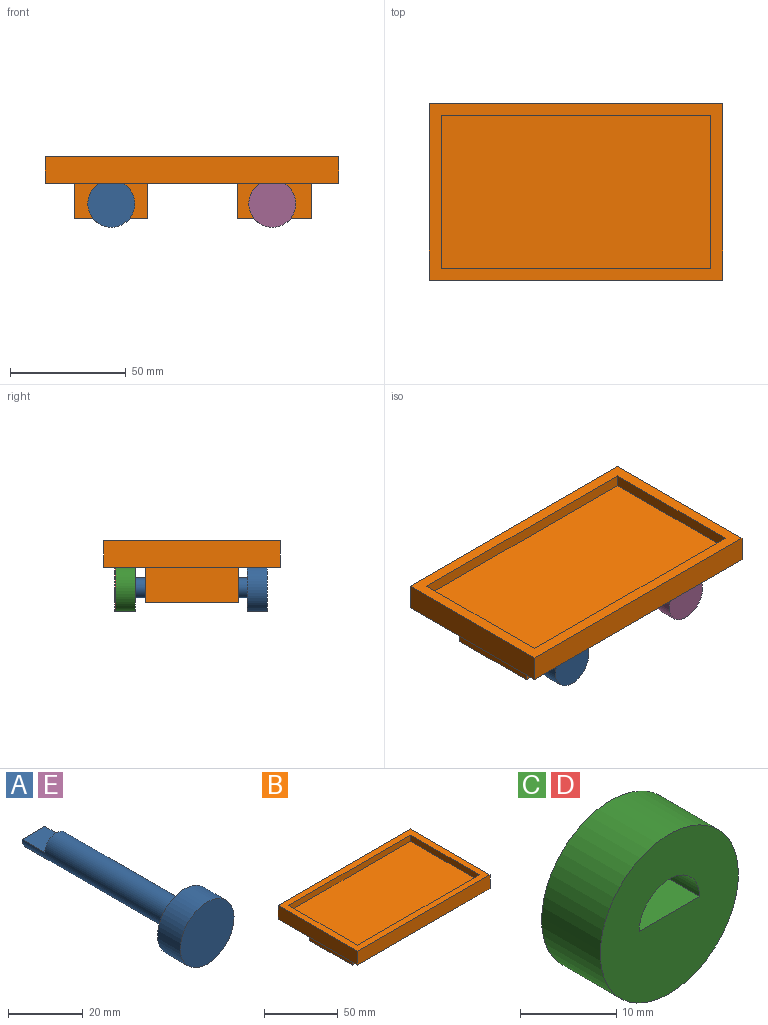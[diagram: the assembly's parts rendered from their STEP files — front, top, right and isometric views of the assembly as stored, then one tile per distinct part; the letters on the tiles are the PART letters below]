
ASSEMBLY  parts=5 mates=4
PART A: 7 faces, bbox 20.3x65.8x20.3 mm
  f0: cylinder r=4.32mm len=57.15mm, axis (0,1,0), area 1433.4mm2, adj f1,f4,f5,f6
  f1: plane 8.64x4.32mm, normal (0,1,0), area 29.3mm2, adj f0,f5
  f2: cylinder r=10.16mm len=20.32mm, axis (0,1,0), area 551.3mm2, adj f3,f4
  f3: plane 20.32x20.32mm, normal (0,-1,0), area 324.3mm2, adj f2
  f4: plane 20.32x20.32mm, normal (0,1,0), area 265.7mm2, adj f0,f2
  f5: plane 8.64x8.64mm, normal (0,0,1), area 74.6mm2, adj f0,f1,f6
  f6: plane 8.64x4.32mm, normal (0,1,0), area 29.3mm2, adj f0,f5
PART B: 27 faces, bbox 127x76.2x26.7 mm
  f0: plane 102.38x17.8mm, normal (0,-1,0), area 1104.7mm2, adj f1,f18,f19,f20,f21,f22,f23,f24
  f1: plane 40.64x17.8mm, normal (-1,0,0), area 723.3mm2, adj f0,f2,f18,f26
  f2: plane 102.38x17.8mm, normal (0,1,0), area 1104.7mm2, adj f1,f18,f19,f20,f21,f22,f23,f24
  f3: plane 127x76.2mm, normal (0,0,-1), area 758.7mm2, adj f4,f5,f6,f7,f14,f15,f16,f17
  f4: plane 127x11.43mm, normal (0,1,0), area 1451.6mm2, adj f3,f5,f7,f12
  f5: plane 76.2x11.43mm, normal (-1,0,0), area 871mm2, adj f3,f4,f6,f12
  f6: plane 127x11.43mm, normal (0,-1,0), area 1451.6mm2, adj f3,f5,f7,f12
  f7: plane 76.2x11.43mm, normal (1,0,0), area 871mm2, adj f3,f4,f6,f12
  f8: plane 116.84x5.08mm, normal (0,-1,0), area 593.5mm2, adj f9,f11,f12,f13
  f9: plane 66.04x5.08mm, normal (-1,0,0), area 335.5mm2, adj f8,f10,f12,f13
  f10: plane 116.84x5.08mm, normal (0,1,0), area 593.5mm2, adj f9,f11,f12,f13
  f11: plane 66.04x5.08mm, normal (1,0,0), area 335.5mm2, adj f8,f10,f12,f13
  f12: plane 127x76.2mm, normal (0,0,1), area 1961.3mm2, adj f4,f5,f6,f7,f8,f9,f10,f11
  f13: plane 116.84x66.04mm, normal (0,0,1), area 7716.1mm2, adj f8,f9,f10,f11
  f14: plane 121.92x2.54mm, normal (0,-1,0), area 309.7mm2, adj f3,f15,f17,f18
  f15: plane 73.15x2.54mm, normal (-1,0,0), area 185.8mm2, adj f3,f14,f16,f18
  f16: plane 121.92x2.54mm, normal (0,1,0), area 309.7mm2, adj f3,f15,f17,f18
  f17: plane 73.15x2.54mm, normal (1,0,0), area 185.8mm2, adj f3,f14,f16,f18
  f18: plane 121.92x73.15mm, normal (0,0,-1), area 4757.9mm2, adj f0,f1,f2,f14,f15,f16,f17,f24
  f19: cylinder r=4.45mm len=40.64mm, axis (0,-1,0), area 1135mm2, adj f0,f2
  f20: plane 40.64x15.26mm, normal (1,0,0), area 620.1mm2, adj f0,f2,f21,f26
  f21: plane 40.64x38.88mm, normal (0,0,-1), area 1580.2mm2, adj f0,f2,f20,f22
  f22: plane 40.64x15.26mm, normal (-1,0,0), area 620.1mm2, adj f0,f2,f21,f25
  f23: cylinder r=4.45mm len=40.64mm, axis (0,-1,0), area 1135mm2, adj f0,f2
  f24: plane 40.64x17.8mm, normal (1,0,0), area 723.3mm2, adj f0,f2,f18,f25
  f25: plane 40.64x31.75mm, normal (0,0,-1), area 1290.3mm2, adj f0,f2,f22,f24
  f26: plane 40.64x31.75mm, normal (0,0,-1), area 1290.3mm2, adj f0,f1,f2,f20
PART C: 5 faces, bbox 20.3x8.6x20.3 mm
  f0: cylinder r=10.16mm len=20.32mm, axis (0,1,0), area 551.3mm2, adj f1,f2
  f1: plane 20.32x20.32mm, normal (0,-1,0), area 293.3mm2, adj f0,f3,f4
  f2: plane 20.32x20.32mm, normal (0,1,0), area 293.3mm2, adj f0,f3,f4
  f3: cylinder r=4.45mm len=8.89mm, axis (0,-1,0), area 120.6mm2, adj f1,f2,f4
  f4: plane 8.89x8.64mm, normal (0,0,1), area 76.8mm2, adj f1,f2,f3
PART D: same geometry as C
PART E: same geometry as A
PLACE A t=(-25.05,-5.65,14.66)mm
PLACE B t=(7.75,-48.96,23.55)mm fixed
PLACE C rot(axis=(1,0,0),180deg) t=(-25.05,-17.61,14.66)mm
PLACE D rot(axis=(1,0,0),180deg) t=(44.63,-17.3,14.66)mm
PLACE E t=(44.63,-5.57,14.66)mm
MATE slider C.f0 <-> A.f0  axis (0,1,0) through (-25.05,-8.98,14.66)mm
MATE slider D.f0 <-> E.f0  axis (0,-1,0) through (44.63,-8.66,14.66)mm
MATE slider B.f19 <-> A.f0  axis (0,-1,0) through (-25.05,-62.39,14.66)mm
MATE slider E.f0 <-> B.f23  axis (0,1,0) through (44.63,-37.32,14.66)mm
